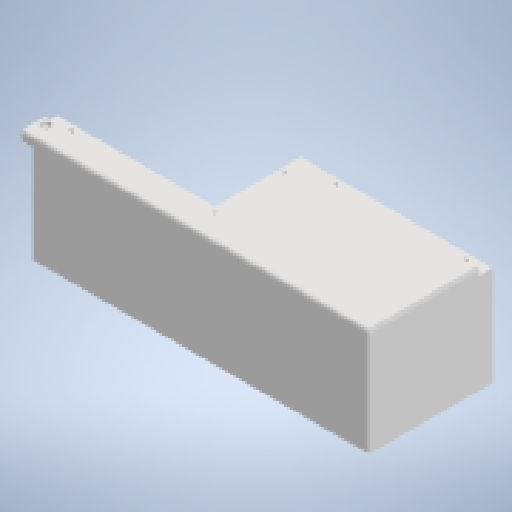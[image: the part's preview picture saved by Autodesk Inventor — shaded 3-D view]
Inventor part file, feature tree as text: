
AUTODESK INVENTOR PART (.ipt)
format: ipt  version: 2025.2 (Build 292293000, 293)  size: 569,344 bytes
history: native  units: mm
features: extrude x12, sketch x12, fillet x2, other x1
ambient origin geometry x8: Origin, YZ Plane, XZ Plane, XY Plane, X Axis, Y Axis, Z Axis, Center Point
bodies: Body1 (feature_tree)
feature tree (27):
  other  "ソリッド1"
  extrude  "押し出し1"  Depth=204.0mm
  extrude  "押し出し2"  Depth=72.0mm
  extrude  "押し出し3"  Depth=7.0mm TaperAngle=0.0deg
  extrude  "押し出し4"  Depth=92.0mm
  extrude  "押し出し5"  TaperAngle=0.0deg  [1 undecoded]
  extrude  "押し出し6"  Depth=8.0mm
  fillet  "フィレット1"  Radius=8.0mm
  extrude  "押し出し7"  Depth=4.0mm TaperAngle=0.0deg
  extrude  "押し出し8"  Depth=3.0mm
  extrude  "押し出し9"  Depth=3.0mm
  extrude  "押し出し10"  Depth=3.0mm
  extrude  "押し出し11"  Depth=12.0mm
  extrude  "押し出し12"  TaperAngle=0.0deg  [1 undecoded]
  fillet  "フィレット2"  Radius=8.0mm
  sketch  "スケッチ1"
  sketch  "スケッチ2"
  sketch  "スケッチ3"
  sketch  "スケッチ4"
  sketch  "スケッチ5"
  sketch  "スケッチ6"
  sketch  "スケッチ7"
  sketch  "スケッチ8"
  sketch  "スケッチ9"
  sketch  "スケッチ10"
  sketch  "スケッチ11"
  sketch  "スケッチ12"
note: 2 required parameter values undecoded (feature->parameter linkage not recoverable at this tier; creation-order binding heuristic only, values carry confidence <= 0.55)
